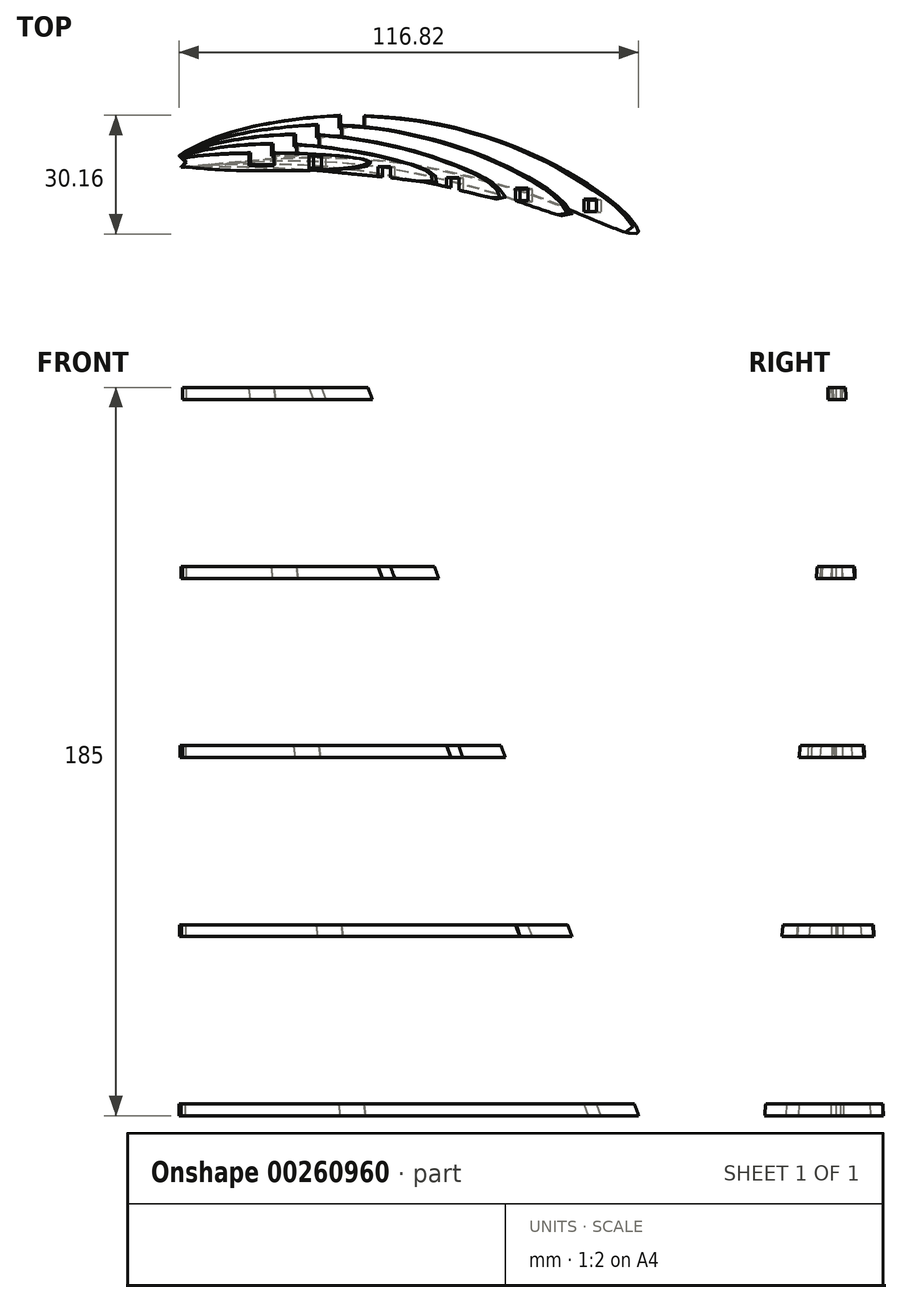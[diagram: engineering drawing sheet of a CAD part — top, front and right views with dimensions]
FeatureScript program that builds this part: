
annotation { "Feature Type Name" : "Feature", "Feature Type Description" : "" }
export const myFeature = defineFeature(function(context is Context, id is Id, definition is map)
    precondition{}
    {
        {
            var Q0;
            Q0=qCreatedBy(makeId("Top.planeOp"),FACE);
            var sketch = newSketch(context, id + "F0", { "sketchPlane" : qUnion([Q0])});
            skLineSegment(sketch, "E0", {"start": v(1.44, 1.44) * mm, "end": v(1.92, 1.72) * mm});
            skLineSegment(sketch, "E1", {"start": v(1.92, 1.72) * mm, "end": v(2.36, 1.99) * mm});
            skLineSegment(sketch, "E2", {"start": v(2.36, 1.99) * mm, "end": v(2.79, 2.25) * mm});
            skLineSegment(sketch, "E3", {"start": v(2.79, 2.25) * mm, "end": v(3.2, 2.5) * mm});
            skLineSegment(sketch, "E4", {"start": v(3.2, 2.5) * mm, "end": v(4, 2.98) * mm});
            skLineSegment(sketch, "E5", {"start": v(4, 2.98) * mm, "end": v(4.43, 3.23) * mm});
            skLineSegment(sketch, "E6", {"start": v(4.43, 3.23) * mm, "end": v(5.66, 3.88) * mm});
            skLineSegment(sketch, "E7", {"start": v(5.66, 3.88) * mm, "end": v(6.55, 4.3) * mm});
            skLineSegment(sketch, "E8", {"start": v(6.55, 4.3) * mm, "end": v(7.46, 4.72) * mm});
            skLineSegment(sketch, "E9", {"start": v(7.46, 4.72) * mm, "end": v(8.73, 5.26) * mm});
            skLineSegment(sketch, "E10", {"start": v(8.73, 5.26) * mm, "end": v(9.3, 5.5) * mm});
            skLineSegment(sketch, "E11", {"start": v(9.3, 5.5) * mm, "end": v(10.22, 5.87) * mm});
            skLineSegment(sketch, "E12", {"start": v(10.22, 5.87) * mm, "end": v(11.14, 6.22) * mm});
            skLineSegment(sketch, "E13", {"start": v(11.14, 6.22) * mm, "end": v(12.07, 6.56) * mm});
            skLineSegment(sketch, "E14", {"start": v(12.07, 6.56) * mm, "end": v(12.99, 6.88) * mm});
            skLineSegment(sketch, "E15", {"start": v(12.99, 6.88) * mm, "end": v(14.24, 7.3) * mm});
            skLineSegment(sketch, "E16", {"start": v(14.24, 7.3) * mm, "end": v(14.85, 7.5) * mm});
            skLineSegment(sketch, "E17", {"start": v(14.85, 7.5) * mm, "end": v(15.79, 7.78) * mm});
            skLineSegment(sketch, "E18", {"start": v(15.79, 7.78) * mm, "end": v(17.68, 8.31) * mm});
            skLineSegment(sketch, "E19", {"start": v(17.68, 8.31) * mm, "end": v(19.6, 8.8) * mm});
            skLineSegment(sketch, "E20", {"start": v(19.6, 8.8) * mm, "end": v(20.82, 9.1) * mm});
            skLineSegment(sketch, "E21", {"start": v(20.82, 9.1) * mm, "end": v(23.44, 9.66) * mm});
            skLineSegment(sketch, "E22", {"start": v(23.44, 9.66) * mm, "end": v(25.37, 10.04) * mm});
            skLineSegment(sketch, "E23", {"start": v(25.37, 10.04) * mm, "end": v(28.23, 10.53) * mm});
            skLineSegment(sketch, "E24", {"start": v(28.23, 10.53) * mm, "end": v(29.26, 10.68) * mm});
            skLineSegment(sketch, "E25", {"start": v(29.26, 10.68) * mm, "end": v(31.2, 10.95) * mm});
            skLineSegment(sketch, "E26", {"start": v(31.2, 10.95) * mm, "end": v(33.16, 11.18) * mm});
            skLineSegment(sketch, "E27", {"start": v(33.16, 11.18) * mm, "end": v(35.12, 11.38) * mm});
            skLineSegment(sketch, "E28", {"start": v(35.12, 11.38) * mm, "end": v(36.25, 11.48) * mm});
            skLineSegment(sketch, "E29", {"start": v(36.25, 11.48) * mm, "end": v(39.05, 11.7) * mm});
            skLineSegment(sketch, "E30", {"start": v(39.05, 11.7) * mm, "end": v(41.01, 11.83) * mm});
            skLineSegment(sketch, "E31", {"start": v(41.01, 11.83) * mm, "end": v(42.98, 11.92) * mm});
            skLineSegment(sketch, "E32", {"start": v(42.98, 11.92) * mm, "end": v(44.74, 11.96) * mm});
            skLineSegment(sketch, "E33", {"start": v(44.74, 11.96) * mm, "end": v(46.91, 11.97) * mm});
            skLineSegment(sketch, "E34", {"start": v(46.91, 11.97) * mm, "end": v(48.88, 11.94) * mm});
            skLineSegment(sketch, "E35", {"start": v(48.88, 11.94) * mm, "end": v(50.85, 11.87) * mm});
            skLineSegment(sketch, "E36", {"start": v(50.85, 11.87) * mm, "end": v(53.48, 11.72) * mm});
            skLineSegment(sketch, "E37", {"start": v(53.48, 11.72) * mm, "end": v(54.78, 11.63) * mm});
            skLineSegment(sketch, "E38", {"start": v(54.78, 11.63) * mm, "end": v(56.74, 11.45) * mm});
            skLineSegment(sketch, "E39", {"start": v(56.74, 11.45) * mm, "end": v(58.7, 11.24) * mm});
            skLineSegment(sketch, "E40", {"start": v(58.7, 11.24) * mm, "end": v(60.65, 11) * mm});
            skLineSegment(sketch, "E41", {"start": v(60.65, 11) * mm, "end": v(62.2, 10.77) * mm});
            skLineSegment(sketch, "E42", {"start": v(62.2, 10.77) * mm, "end": v(64.54, 10.39) * mm});
            skLineSegment(sketch, "E43", {"start": v(64.54, 10.39) * mm, "end": v(66.48, 10.03) * mm});
            skLineSegment(sketch, "E44", {"start": v(66.48, 10.03) * mm, "end": v(68.41, 9.64) * mm});
            skLineSegment(sketch, "E45", {"start": v(68.41, 9.64) * mm, "end": v(70.94, 9.1) * mm});
            skLineSegment(sketch, "E46", {"start": v(70.94, 9.1) * mm, "end": v(72.26, 8.78) * mm});
            skLineSegment(sketch, "E47", {"start": v(72.26, 8.78) * mm, "end": v(74.17, 8.31) * mm});
            skLineSegment(sketch, "E48", {"start": v(74.17, 8.31) * mm, "end": v(76.07, 7.8) * mm});
            skLineSegment(sketch, "E49", {"start": v(76.07, 7.8) * mm, "end": v(77.96, 7.27) * mm});
            skLineSegment(sketch, "E50", {"start": v(77.96, 7.27) * mm, "end": v(79.44, 6.82) * mm});
            skLineSegment(sketch, "E51", {"start": v(79.44, 6.82) * mm, "end": v(81.71, 6.07) * mm});
            skLineSegment(sketch, "E52", {"start": v(81.71, 6.07) * mm, "end": v(83.57, 5.42) * mm});
            skLineSegment(sketch, "E53", {"start": v(83.57, 5.42) * mm, "end": v(85.42, 4.73) * mm});
            skLineSegment(sketch, "E54", {"start": v(85.42, 4.73) * mm, "end": v(87.45, 3.95) * mm});
            skLineSegment(sketch, "E55", {"start": v(87.45, 3.95) * mm, "end": v(89.08, 3.3) * mm});
            skLineSegment(sketch, "E56", {"start": v(89.08, 3.3) * mm, "end": v(90.9, 2.53) * mm});
            skLineSegment(sketch, "E57", {"start": v(90.9, 2.53) * mm, "end": v(92.7, 1.74) * mm});
            skLineSegment(sketch, "E58", {"start": v(92.7, 1.74) * mm, "end": v(94.87, 0.72) * mm});
            skLineSegment(sketch, "E59", {"start": v(94.87, 0.72) * mm, "end": v(95.37, 0.47) * mm});
            skLineSegment(sketch, "E60", {"start": v(95.37, 0.47) * mm, "end": v(96.24, 0.02) * mm});
            skLineSegment(sketch, "E61", {"start": v(96.24, 0.02) * mm, "end": v(97.98, -0.9) * mm});
            skLineSegment(sketch, "E62", {"start": v(97.98, -0.9) * mm, "end": v(99.7, -1.86) * mm});
            skLineSegment(sketch, "E63", {"start": v(99.7, -1.86) * mm, "end": v(101.45, -2.87) * mm});
            skLineSegment(sketch, "E64", {"start": v(101.45, -2.87) * mm, "end": v(103.1, -3.86) * mm});
            skLineSegment(sketch, "E65", {"start": v(103.1, -3.86) * mm, "end": v(104.78, -4.9) * mm});
            skLineSegment(sketch, "E66", {"start": v(104.78, -4.9) * mm, "end": v(107.19, -6.46) * mm});
            skLineSegment(sketch, "E67", {"start": v(107.19, -6.46) * mm, "end": v(108.06, -7.05) * mm});
            skLineSegment(sketch, "E68", {"start": v(108.06, -7.05) * mm, "end": v(109.65, -8.19) * mm});
            skLineSegment(sketch, "E69", {"start": v(109.65, -8.19) * mm, "end": v(111.97, -9.93) * mm});
            skLineSegment(sketch, "E70", {"start": v(111.97, -9.93) * mm, "end": v(112.82, -10.59) * mm});
            skLineSegment(sketch, "E71", {"start": v(112.82, -10.59) * mm, "end": v(113.6, -11.22) * mm});
            skLineSegment(sketch, "E72", {"start": v(113.6, -11.22) * mm, "end": v(114.35, -11.87) * mm});
            skLineSegment(sketch, "E73", {"start": v(114.35, -11.87) * mm, "end": v(114.71, -12.2) * mm});
            skLineSegment(sketch, "E74", {"start": v(114.71, -12.2) * mm, "end": v(115.06, -12.53) * mm});
            skLineSegment(sketch, "E75", {"start": v(115.06, -12.53) * mm, "end": v(115.4, -12.86) * mm});
            skLineSegment(sketch, "E76", {"start": v(115.4, -12.86) * mm, "end": v(115.56, -13.04) * mm});
            skLineSegment(sketch, "E77", {"start": v(115.56, -13.04) * mm, "end": v(116.33, -13.9) * mm});
            skLineSegment(sketch, "E78", {"start": v(116.33, -13.9) * mm, "end": v(116.63, -14.27) * mm});
            skLineSegment(sketch, "E79", {"start": v(116.63, -14.27) * mm, "end": v(116.94, -14.64) * mm});
            skLineSegment(sketch, "E80", {"start": v(116.94, -14.64) * mm, "end": v(117.27, -15.03) * mm});
            skLineSegment(sketch, "E81", {"start": v(117.27, -15.03) * mm, "end": v(117.62, -15.43) * mm});
            skLineSegment(sketch, "E82", {"start": v(117.62, -15.43) * mm, "end": v(117.84, -15.67) * mm});
            skLineSegment(sketch, "E83", {"start": v(117.84, -15.67) * mm, "end": v(118.38, -16.28) * mm});
            skLineSegment(sketch, "E84", {"start": v(118.38, -16.28) * mm, "end": v(118.54, -16.5) * mm});
            skLineSegment(sketch, "E85", {"start": v(118.54, -16.5) * mm, "end": v(118.68, -16.72) * mm});
            skLineSegment(sketch, "E86", {"start": v(118.68, -16.72) * mm, "end": v(118.78, -16.94) * mm});
            skLineSegment(sketch, "E87", {"start": v(118.78, -16.94) * mm, "end": v(118.8, -17.05) * mm});
            skLineSegment(sketch, "E88", {"start": v(118.8, -17.05) * mm, "end": v(118.83, -17.16) * mm});
            skLineSegment(sketch, "E89", {"start": v(118.83, -17.16) * mm, "end": v(118.83, -17.27) * mm});
            skLineSegment(sketch, "E90", {"start": v(118.83, -17.27) * mm, "end": v(118.82, -17.37) * mm});
            skLineSegment(sketch, "E91", {"start": v(118.82, -17.37) * mm, "end": v(118.8, -17.47) * mm});
            skLineSegment(sketch, "E92", {"start": v(118.8, -17.47) * mm, "end": v(118.74, -17.59) * mm});
            skLineSegment(sketch, "E93", {"start": v(118.74, -17.59) * mm, "end": v(118.68, -17.7) * mm});
            skLineSegment(sketch, "E94", {"start": v(118.68, -17.7) * mm, "end": v(118.6, -17.8) * mm});
            skLineSegment(sketch, "E95", {"start": v(118.6, -17.8) * mm, "end": v(118.42, -17.97) * mm});
            skLineSegment(sketch, "E96", {"start": v(118.42, -17.97) * mm, "end": v(118.2, -18.12) * mm});
            skLineSegment(sketch, "E97", {"start": v(118.2, -18.12) * mm, "end": v(118.08, -18.18) * mm});
            skLineSegment(sketch, "E98", {"start": v(118.08, -18.18) * mm, "end": v(117.74, -18.28) * mm});
            skLineSegment(sketch, "E99", {"start": v(117.74, -18.28) * mm, "end": v(117.5, -18.3) * mm});
            skLineSegment(sketch, "E100", {"start": v(117.5, -18.3) * mm, "end": v(117.26, -18.27) * mm});
            skLineSegment(sketch, "E101", {"start": v(117.26, -18.27) * mm, "end": v(117.02, -18.22) * mm});
            skLineSegment(sketch, "E102", {"start": v(117.02, -18.22) * mm, "end": v(116.78, -18.14) * mm});
            skLineSegment(sketch, "E103", {"start": v(116.78, -18.14) * mm, "end": v(116.53, -18.04) * mm});
            skLineSegment(sketch, "E104", {"start": v(116.53, -18.04) * mm, "end": v(115.8, -17.7) * mm});
            skLineSegment(sketch, "E105", {"start": v(115.8, -17.7) * mm, "end": v(115.08, -17.39) * mm});
            skLineSegment(sketch, "E106", {"start": v(115.08, -17.39) * mm, "end": v(114.61, -17.2) * mm});
            skLineSegment(sketch, "E107", {"start": v(114.61, -17.2) * mm, "end": v(113.69, -16.86) * mm});
            skLineSegment(sketch, "E108", {"start": v(113.69, -16.86) * mm, "end": v(112.78, -16.55) * mm});
            skLineSegment(sketch, "E109", {"start": v(112.78, -16.55) * mm, "end": v(111.62, -16.15) * mm});
            skLineSegment(sketch, "E110", {"start": v(111.62, -16.15) * mm, "end": v(110.97, -15.92) * mm});
            skLineSegment(sketch, "E111", {"start": v(110.97, -15.92) * mm, "end": v(110.06, -15.57) * mm});
            skLineSegment(sketch, "E112", {"start": v(110.06, -15.57) * mm, "end": v(109.16, -15.2) * mm});
            skLineSegment(sketch, "E113", {"start": v(109.16, -15.2) * mm, "end": v(107.33, -14.42) * mm});
            skLineSegment(sketch, "E114", {"start": v(107.33, -14.42) * mm, "end": v(105.28, -13.52) * mm});
            skLineSegment(sketch, "E115", {"start": v(105.28, -13.52) * mm, "end": v(103.7, -12.84) * mm});
            skLineSegment(sketch, "E116", {"start": v(103.7, -12.84) * mm, "end": v(101.88, -12.07) * mm});
            skLineSegment(sketch, "E117", {"start": v(101.88, -12.07) * mm, "end": v(100.06, -11.33) * mm});
            skLineSegment(sketch, "E118", {"start": v(100.06, -11.33) * mm, "end": v(98.23, -10.6) * mm});
            skLineSegment(sketch, "E119", {"start": v(98.23, -10.6) * mm, "end": v(96.78, -10.05) * mm});
            skLineSegment(sketch, "E120", {"start": v(96.78, -10.05) * mm, "end": v(94.55, -9.23) * mm});
            skLineSegment(sketch, "E121", {"start": v(94.55, -9.23) * mm, "end": v(92.7, -8.57) * mm});
            skLineSegment(sketch, "E122", {"start": v(92.7, -8.57) * mm, "end": v(90.84, -7.93) * mm});
            skLineSegment(sketch, "E123", {"start": v(90.84, -7.93) * mm, "end": v(88.96, -7.31) * mm});
            skLineSegment(sketch, "E124", {"start": v(88.96, -7.31) * mm, "end": v(86.25, -6.46) * mm});
            skLineSegment(sketch, "E125", {"start": v(86.25, -6.46) * mm, "end": v(85.2, -6.14) * mm});
            skLineSegment(sketch, "E126", {"start": v(85.2, -6.14) * mm, "end": v(83.31, -5.58) * mm});
            skLineSegment(sketch, "E127", {"start": v(83.31, -5.58) * mm, "end": v(81.42, -5.04) * mm});
            skLineSegment(sketch, "E128", {"start": v(81.42, -5.04) * mm, "end": v(79.52, -4.52) * mm});
            skLineSegment(sketch, "E129", {"start": v(79.52, -4.52) * mm, "end": v(77.62, -4.02) * mm});
            skLineSegment(sketch, "E130", {"start": v(77.62, -4.02) * mm, "end": v(75.7, -3.54) * mm});
            skLineSegment(sketch, "E131", {"start": v(75.7, -3.54) * mm, "end": v(73.93, -3.11) * mm});
            skLineSegment(sketch, "E132", {"start": v(73.93, -3.11) * mm, "end": v(71.88, -2.64) * mm});
            skLineSegment(sketch, "E133", {"start": v(71.88, -2.64) * mm, "end": v(69.95, -2.21) * mm});
            skLineSegment(sketch, "E134", {"start": v(69.95, -2.21) * mm, "end": v(68.03, -1.81) * mm});
            skLineSegment(sketch, "E135", {"start": v(68.03, -1.81) * mm, "end": v(66.1, -1.43) * mm});
            skLineSegment(sketch, "E136", {"start": v(66.1, -1.43) * mm, "end": v(64.16, -1.08) * mm});
            skLineSegment(sketch, "E137", {"start": v(64.16, -1.08) * mm, "end": v(62.22, -0.75) * mm});
            skLineSegment(sketch, "E138", {"start": v(62.22, -0.75) * mm, "end": v(60.53, -0.48) * mm});
            skLineSegment(sketch, "E139", {"start": v(60.53, -0.48) * mm, "end": v(58.32, -0.16) * mm});
            skLineSegment(sketch, "E140", {"start": v(58.32, -0.16) * mm, "end": v(56.37, 0.1) * mm});
            skLineSegment(sketch, "E141", {"start": v(56.37, 0.1) * mm, "end": v(54.41, 0.33) * mm});
            skLineSegment(sketch, "E142", {"start": v(54.41, 0.33) * mm, "end": v(52.46, 0.54) * mm});
            skLineSegment(sketch, "E143", {"start": v(52.46, 0.54) * mm, "end": v(50.5, 0.72) * mm});
            skLineSegment(sketch, "E144", {"start": v(50.5, 0.72) * mm, "end": v(48.53, 0.87) * mm});
            skLineSegment(sketch, "E145", {"start": v(48.53, 0.87) * mm, "end": v(47.13, 0.96) * mm});
            skLineSegment(sketch, "E146", {"start": v(47.13, 0.96) * mm, "end": v(44.6, 1.09) * mm});
            skLineSegment(sketch, "E147", {"start": v(44.6, 1.09) * mm, "end": v(42.63, 1.15) * mm});
            skLineSegment(sketch, "E148", {"start": v(42.63, 1.15) * mm, "end": v(40.66, 1.2) * mm});
            skLineSegment(sketch, "E149", {"start": v(40.66, 1.2) * mm, "end": v(38.7, 1.22) * mm});
            skLineSegment(sketch, "E150", {"start": v(38.7, 1.22) * mm, "end": v(36.73, 1.22) * mm});
            skLineSegment(sketch, "E151", {"start": v(36.73, 1.22) * mm, "end": v(34.33, 1.2) * mm});
            skLineSegment(sketch, "E152", {"start": v(34.33, 1.2) * mm, "end": v(32.79, 1.17) * mm});
            skLineSegment(sketch, "E153", {"start": v(32.79, 1.17) * mm, "end": v(30.82, 1.11) * mm});
            skLineSegment(sketch, "E154", {"start": v(30.82, 1.11) * mm, "end": v(28.85, 1.04) * mm});
            skLineSegment(sketch, "E155", {"start": v(28.85, 1.04) * mm, "end": v(26.88, 0.94) * mm});
            skLineSegment(sketch, "E156", {"start": v(26.88, 0.94) * mm, "end": v(24.92, 0.83) * mm});
            skLineSegment(sketch, "E157", {"start": v(24.92, 0.83) * mm, "end": v(23.2, 0.72) * mm});
            skLineSegment(sketch, "E158", {"start": v(23.2, 0.72) * mm, "end": v(21, 0.55) * mm});
            skLineSegment(sketch, "E159", {"start": v(21, 0.55) * mm, "end": v(19.04, 0.38) * mm});
            skLineSegment(sketch, "E160", {"start": v(19.04, 0.38) * mm, "end": v(17.08, 0.2) * mm});
            skLineSegment(sketch, "E161", {"start": v(17.08, 0.2) * mm, "end": v(15.12, -0.01) * mm});
            skLineSegment(sketch, "E162", {"start": v(15.12, -0.01) * mm, "end": v(14.12, -0.12) * mm});
            skLineSegment(sketch, "E163", {"start": v(14.12, -0.12) * mm, "end": v(11.18, -0.45) * mm});
            skLineSegment(sketch, "E164", {"start": v(11.18, -0.45) * mm, "end": v(9.22, -0.66) * mm});
            skLineSegment(sketch, "E165", {"start": v(9.22, -0.66) * mm, "end": v(7.3, -0.84) * mm});
            skLineSegment(sketch, "E166", {"start": v(7.3, -0.84) * mm, "end": v(5.37, -0.99) * mm});
            skLineSegment(sketch, "E167", {"start": v(5.37, -0.99) * mm, "end": v(4.4, -1.06) * mm});
            skLineSegment(sketch, "E168", {"start": v(4.4, -1.06) * mm, "end": v(3.4, -1.14) * mm});
            skLineSegment(sketch, "E169", {"start": v(3.4, -1.14) * mm, "end": v(2.75, -1.2) * mm});
            skLineSegment(sketch, "E170", {"start": v(2.75, -1.2) * mm, "end": v(1.83, -1.25) * mm});
            skLineSegment(sketch, "E171", {"start": v(1.83, -1.25) * mm, "end": v(1.57, -1.25) * mm});
            skLineSegment(sketch, "E172", {"start": v(1.57, -1.25) * mm, "end": v(1.33, -1.22) * mm});
            skLineSegment(sketch, "E173", {"start": v(1.33, -1.22) * mm, "end": v(1.09, -1.16) * mm});
            skLineSegment(sketch, "E174", {"start": v(1.09, -1.16) * mm, "end": v(0.86, -1.08) * mm});
            skLineSegment(sketch, "E175", {"start": v(0.86, -1.08) * mm, "end": v(0.64, -0.96) * mm});
            skLineSegment(sketch, "E176", {"start": v(0.64, -0.96) * mm, "end": v(0.48, -0.84) * mm});
            skLineSegment(sketch, "E177", {"start": v(0.48, -0.84) * mm, "end": v(0.27, -0.62) * mm});
            skLineSegment(sketch, "E178", {"start": v(0.27, -0.62) * mm, "end": v(0.13, -0.4) * mm});
            skLineSegment(sketch, "E179", {"start": v(0.13, -0.4) * mm, "end": v(0.07, -0.28) * mm});
            skLineSegment(sketch, "E180", {"start": v(0.07, -0.28) * mm, "end": v(0.03, -0.17) * mm});
            skLineSegment(sketch, "E181", {"start": v(0.03, -0.17) * mm, "end": v(0, 0) * mm});
            skLineSegment(sketch, "E182", {"start": v(0, 0) * mm, "end": v(0, 0.05) * mm});
            skLineSegment(sketch, "E183", {"start": v(0, 0.05) * mm, "end": v(0, 0.16) * mm});
            skLineSegment(sketch, "E184", {"start": v(0, 0.16) * mm, "end": v(0.04, 0.26) * mm});
            skLineSegment(sketch, "E185", {"start": v(0.04, 0.26) * mm, "end": v(0.08, 0.36) * mm});
            skLineSegment(sketch, "E186", {"start": v(0.08, 0.36) * mm, "end": v(0.13, 0.46) * mm});
            skLineSegment(sketch, "E187", {"start": v(0.13, 0.46) * mm, "end": v(0.28, 0.65) * mm});
            skLineSegment(sketch, "E188", {"start": v(0.28, 0.65) * mm, "end": v(0.47, 0.82) * mm});
            skLineSegment(sketch, "E189", {"start": v(0.47, 0.82) * mm, "end": v(0.7, 0.98) * mm});
            skLineSegment(sketch, "E190", {"start": v(0.7, 0.98) * mm, "end": v(0.93, 1.14) * mm});
            skLineSegment(sketch, "E191", {"start": v(0.93, 1.14) * mm, "end": v(1.44, 1.44) * mm});
            skSolve(sketch);
        }
        {
            var Q0;
            Q0=qCreatedBy(makeId("Top.planeOp"),FACE);
            var sketch = newSketch(context, id + "F1", { "sketchPlane" : qUnion([Q0])});
            skPoint(sketch, "E192.0", {"position": v(0, 0) * mm});
            skPoint(sketch, "E192.1", {"position": v(0, 0.16) * mm});
            skPoint(sketch, "E192.2", {"position": v(0.13, 0.46) * mm});
            skPoint(sketch, "E192.3", {"position": v(1.44, 1.44) * mm});
            skPoint(sketch, "E192.4", {"position": v(10.22, 5.87) * mm});
            skPoint(sketch, "E192.5", {"position": v(23.44, 9.66) * mm});
            skPoint(sketch, "E192.6", {"position": v(36.25, 11.48) * mm});
            skPoint(sketch, "E192.7", {"position": v(46.91, 11.97) * mm});
            skPoint(sketch, "E192.8", {"position": v(64.54, 10.39) * mm});
            skPoint(sketch, "E192.9", {"position": v(79.44, 6.82) * mm});
            skPoint(sketch, "E192.10", {"position": v(101.45, -2.87) * mm});
            skPoint(sketch, "E192.11", {"position": v(108.06, -7.05) * mm});
            skPoint(sketch, "E192.12", {"position": v(118.8, -17.47) * mm});
            skPoint(sketch, "E192.13", {"position": v(118.6, -17.8) * mm});
            skPoint(sketch, "E192.14", {"position": v(118.08, -18.18) * mm});
            skPoint(sketch, "E192.15", {"position": v(96.78, -10.05) * mm});
            skPoint(sketch, "E192.16", {"position": v(83.31, -5.58) * mm});
            skPoint(sketch, "E192.17", {"position": v(66.1, -1.43) * mm});
            skPoint(sketch, "E192.18", {"position": v(52.46, 0.54) * mm});
            skPoint(sketch, "E192.19", {"position": v(36.73, 1.22) * mm});
            skPoint(sketch, "E192.20", {"position": v(24.92, 0.83) * mm});
            skPoint(sketch, "E192.21", {"position": v(11.18, -0.45) * mm});
            skPoint(sketch, "E192.22", {"position": v(0.64, -0.96) * mm});
            skPoint(sketch, "E192.23", {"position": v(0.13, -0.4) * mm});
            skPoint(sketch, "E192.24", {"position": v(0.03, -0.17) * mm});
            skPoint(sketch, "E192.25", {"position": v(91.8, 2.14) * mm});
            skPoint(sketch, "E192.26", {"position": v(115.48, -12.95) * mm});
            skPoint(sketch, "E192.27", {"position": v(110.52, -15.74) * mm});
            skPoint(sketch, "E192.28", {"position": v(1.7, -1.25) * mm});
            skFitSpline(sketch, "E193", {"points": [v(0, 0) * mm, v(0, 0.16) * mm, v(0.13, 0.46) * mm, v(1.44, 1.44) * mm, v(10.22, 5.87) * mm, v(23.44, 9.66) * mm, v(36.25, 11.48) * mm, v(46.91, 11.97) * mm, v(64.54, 10.39) * mm, v(79.44, 6.82) * mm, v(91.8, 2.14) * mm, v(101.45, -2.87) * mm, v(108.06, -7.05) * mm, v(115.48, -12.95) * mm, v(118.8, -17.47) * mm, v(118.6, -17.8) * mm, v(118.08, -18.18) * mm, v(110.52, -15.74) * mm, v(96.78, -10.05) * mm, v(83.31, -5.58) * mm, v(66.1, -1.43) * mm, v(52.46, 0.54) * mm, v(36.73, 1.22) * mm, v(24.92, 0.83) * mm, v(11.18, -0.45) * mm, v(1.7, -1.25) * mm, v(0.64, -1.04) * mm, v(0.13, -0.4) * mm, v(0.03, -0.17) * mm, v(0, 0) * mm]});
            skSolve(sketch);
        }
        {
            var Q0;
            Q0=qCreatedBy(makeId("Top.planeOp"),FACE);
            cPlane(context, id + "F2", {"entities" : qUnion([Q0]), "cplaneType" : CPlaneType.OFFSET, "offset" : 185 * mm, "width" : 150 * mm, "height" : 150 * mm});
        }
        {
            var Q0;
            Q0=qCreatedBy(id+"F2.planeOp",FACE);
            var sketch = newSketch(context, id + "F3", { "sketchPlane" : qUnion([Q0])});
            skLineSegment(sketch, "E194", {"start": v(0, 0) * mm, "end": v(0.13, 0.15) * mm});
            skLineSegment(sketch, "E195", {"start": v(0.13, 0.15) * mm, "end": v(0.27, 0.3) * mm});
            skLineSegment(sketch, "E196", {"start": v(0.27, 0.3) * mm, "end": v(0.34, 0.36) * mm});
            skLineSegment(sketch, "E197", {"start": v(0.34, 0.36) * mm, "end": v(0.4, 0.4) * mm});
            skLineSegment(sketch, "E198", {"start": v(0.4, 0.4) * mm, "end": v(0.5, 0.47) * mm});
            skLineSegment(sketch, "E199", {"start": v(0.5, 0.47) * mm, "end": v(0.59, 0.52) * mm});
            skLineSegment(sketch, "E200", {"start": v(0.59, 0.52) * mm, "end": v(0.67, 0.56) * mm});
            skLineSegment(sketch, "E201", {"start": v(0.67, 0.56) * mm, "end": v(0.76, 0.6) * mm});
            skLineSegment(sketch, "E202", {"start": v(0.76, 0.6) * mm, "end": v(0.95, 0.66) * mm});
            skLineSegment(sketch, "E203", {"start": v(0.95, 0.66) * mm, "end": v(1.15, 0.71) * mm});
            skLineSegment(sketch, "E204", {"start": v(1.15, 0.71) * mm, "end": v(1.54, 0.8) * mm});
            skLineSegment(sketch, "E205", {"start": v(1.54, 0.8) * mm, "end": v(1.74, 0.84) * mm});
            skLineSegment(sketch, "E206", {"start": v(1.74, 0.84) * mm, "end": v(2.14, 0.91) * mm});
            skLineSegment(sketch, "E207", {"start": v(2.14, 0.91) * mm, "end": v(2.9, 1.06) * mm});
            skLineSegment(sketch, "E208", {"start": v(2.9, 1.06) * mm, "end": v(3.39, 1.15) * mm});
            skLineSegment(sketch, "E209", {"start": v(3.39, 1.15) * mm, "end": v(4.46, 1.31) * mm});
            skLineSegment(sketch, "E210", {"start": v(4.46, 1.31) * mm, "end": v(5.25, 1.41) * mm});
            skLineSegment(sketch, "E211", {"start": v(5.25, 1.41) * mm, "end": v(5.93, 1.5) * mm});
            skLineSegment(sketch, "E212", {"start": v(5.93, 1.5) * mm, "end": v(6.82, 1.6) * mm});
            skLineSegment(sketch, "E213", {"start": v(6.82, 1.6) * mm, "end": v(7.6, 1.67) * mm});
            skLineSegment(sketch, "E214", {"start": v(7.6, 1.67) * mm, "end": v(9.01, 1.8) * mm});
            skLineSegment(sketch, "E215", {"start": v(9.01, 1.8) * mm, "end": v(10.76, 1.93) * mm});
            skLineSegment(sketch, "E216", {"start": v(10.76, 1.93) * mm, "end": v(11.55, 1.98) * mm});
            skLineSegment(sketch, "E217", {"start": v(11.55, 1.98) * mm, "end": v(12.55, 2.04) * mm});
            skLineSegment(sketch, "E218", {"start": v(12.55, 2.04) * mm, "end": v(13.13, 2.07) * mm});
            skLineSegment(sketch, "E219", {"start": v(13.13, 2.07) * mm, "end": v(13.92, 2.1) * mm});
            skLineSegment(sketch, "E220", {"start": v(13.92, 2.1) * mm, "end": v(15.5, 2.16) * mm});
            skLineSegment(sketch, "E221", {"start": v(15.5, 2.16) * mm, "end": v(16.48, 2.2) * mm});
            skLineSegment(sketch, "E222", {"start": v(16.48, 2.2) * mm, "end": v(18.66, 2.25) * mm});
            skLineSegment(sketch, "E223", {"start": v(18.66, 2.25) * mm, "end": v(20.72, 2.3) * mm});
            skLineSegment(sketch, "E224", {"start": v(20.72, 2.3) * mm, "end": v(23.4, 2.33) * mm});
            skLineSegment(sketch, "E225", {"start": v(23.4, 2.33) * mm, "end": v(25, 2.34) * mm});
            skLineSegment(sketch, "E226", {"start": v(25, 2.34) * mm, "end": v(26.56, 2.33) * mm});
            skLineSegment(sketch, "E227", {"start": v(26.56, 2.33) * mm, "end": v(29.28, 2.3) * mm});
            skLineSegment(sketch, "E228", {"start": v(29.28, 2.3) * mm, "end": v(31.3, 2.25) * mm});
            skLineSegment(sketch, "E229", {"start": v(31.3, 2.25) * mm, "end": v(33.52, 2.2) * mm});
            skLineSegment(sketch, "E230", {"start": v(33.52, 2.2) * mm, "end": v(34.46, 2.16) * mm});
            skLineSegment(sketch, "E231", {"start": v(34.46, 2.16) * mm, "end": v(36.04, 2.1) * mm});
            skLineSegment(sketch, "E232", {"start": v(36.04, 2.1) * mm, "end": v(36.83, 2.07) * mm});
            skLineSegment(sketch, "E233", {"start": v(36.83, 2.07) * mm, "end": v(37.45, 2.04) * mm});
            skLineSegment(sketch, "E234", {"start": v(37.45, 2.04) * mm, "end": v(38.41, 1.99) * mm});
            skLineSegment(sketch, "E235", {"start": v(38.41, 1.99) * mm, "end": v(39.2, 1.93) * mm});
            skLineSegment(sketch, "E236", {"start": v(39.2, 1.93) * mm, "end": v(40.99, 1.8) * mm});
            skLineSegment(sketch, "E237", {"start": v(40.99, 1.8) * mm, "end": v(42.35, 1.67) * mm});
            skLineSegment(sketch, "E238", {"start": v(42.35, 1.67) * mm, "end": v(43.14, 1.6) * mm});
            skLineSegment(sketch, "E239", {"start": v(43.14, 1.6) * mm, "end": v(44.08, 1.5) * mm});
            skLineSegment(sketch, "E240", {"start": v(44.08, 1.5) * mm, "end": v(44.7, 1.42) * mm});
            skLineSegment(sketch, "E241", {"start": v(44.7, 1.42) * mm, "end": v(45.49, 1.32) * mm});
            skLineSegment(sketch, "E242", {"start": v(45.49, 1.32) * mm, "end": v(46.61, 1.15) * mm});
            skLineSegment(sketch, "E243", {"start": v(46.61, 1.15) * mm, "end": v(47.06, 1.07) * mm});
            skLineSegment(sketch, "E244", {"start": v(47.06, 1.07) * mm, "end": v(47.46, 1) * mm});
            skLineSegment(sketch, "E245", {"start": v(47.46, 1) * mm, "end": v(47.85, 0.92) * mm});
            skLineSegment(sketch, "E246", {"start": v(47.85, 0.92) * mm, "end": v(48.23, 0.84) * mm});
            skLineSegment(sketch, "E247", {"start": v(48.23, 0.84) * mm, "end": v(48.46, 0.8) * mm});
            skLineSegment(sketch, "E248", {"start": v(48.46, 0.8) * mm, "end": v(48.78, 0.72) * mm});
            skLineSegment(sketch, "E249", {"start": v(48.78, 0.72) * mm, "end": v(48.96, 0.68) * mm});
            skLineSegment(sketch, "E250", {"start": v(48.96, 0.68) * mm, "end": v(49.14, 0.61) * mm});
            skLineSegment(sketch, "E251", {"start": v(49.14, 0.61) * mm, "end": v(49.33, 0.54) * mm});
            skLineSegment(sketch, "E252", {"start": v(49.33, 0.54) * mm, "end": v(49.43, 0.5) * mm});
            skLineSegment(sketch, "E253", {"start": v(49.43, 0.5) * mm, "end": v(49.53, 0.44) * mm});
            skLineSegment(sketch, "E254", {"start": v(49.53, 0.44) * mm, "end": v(49.6, 0.4) * mm});
            skLineSegment(sketch, "E255", {"start": v(49.6, 0.4) * mm, "end": v(49.73, 0.32) * mm});
            skLineSegment(sketch, "E256", {"start": v(49.73, 0.32) * mm, "end": v(49.83, 0.25) * mm});
            skLineSegment(sketch, "E257", {"start": v(49.83, 0.25) * mm, "end": v(49.91, 0.18) * mm});
            skLineSegment(sketch, "E258", {"start": v(49.91, 0.18) * mm, "end": v(49.94, 0.14) * mm});
            skLineSegment(sketch, "E259", {"start": v(49.94, 0.14) * mm, "end": v(49.97, 0.1) * mm});
            skLineSegment(sketch, "E260", {"start": v(49.97, 0.1) * mm, "end": v(49.99, 0.07) * mm});
            skLineSegment(sketch, "E261", {"start": v(49.99, 0.07) * mm, "end": v(50, 0.03) * mm});
            skLineSegment(sketch, "E262", {"start": v(50, 0.03) * mm, "end": v(50, 0) * mm});
            skLineSegment(sketch, "E263", {"start": v(50, 0) * mm, "end": v(50, -0.04) * mm});
            skLineSegment(sketch, "E264", {"start": v(50, -0.04) * mm, "end": v(49.97, -0.08) * mm});
            skLineSegment(sketch, "E265", {"start": v(49.97, -0.08) * mm, "end": v(49.95, -0.11) * mm});
            skLineSegment(sketch, "E266", {"start": v(49.95, -0.11) * mm, "end": v(49.92, -0.15) * mm});
            skLineSegment(sketch, "E267", {"start": v(49.92, -0.15) * mm, "end": v(49.88, -0.18) * mm});
            skLineSegment(sketch, "E268", {"start": v(49.88, -0.18) * mm, "end": v(49.79, -0.24) * mm});
            skLineSegment(sketch, "E269", {"start": v(49.79, -0.24) * mm, "end": v(49.69, -0.3) * mm});
            skLineSegment(sketch, "E270", {"start": v(49.69, -0.3) * mm, "end": v(49.6, -0.35) * mm});
            skLineSegment(sketch, "E271", {"start": v(49.6, -0.35) * mm, "end": v(49.48, -0.41) * mm});
            skLineSegment(sketch, "E272", {"start": v(49.48, -0.41) * mm, "end": v(49.38, -0.46) * mm});
            skLineSegment(sketch, "E273", {"start": v(49.38, -0.46) * mm, "end": v(49.19, -0.54) * mm});
            skLineSegment(sketch, "E274", {"start": v(49.19, -0.54) * mm, "end": v(49, -0.6) * mm});
            skLineSegment(sketch, "E275", {"start": v(49, -0.6) * mm, "end": v(48.83, -0.66) * mm});
            skLineSegment(sketch, "E276", {"start": v(48.83, -0.66) * mm, "end": v(48.5, -0.75) * mm});
            skLineSegment(sketch, "E277", {"start": v(48.5, -0.75) * mm, "end": v(48.29, -0.8) * mm});
            skLineSegment(sketch, "E278", {"start": v(48.29, -0.8) * mm, "end": v(47.9, -0.88) * mm});
            skLineSegment(sketch, "E279", {"start": v(47.9, -0.88) * mm, "end": v(47.52, -0.96) * mm});
            skLineSegment(sketch, "E280", {"start": v(47.52, -0.96) * mm, "end": v(47.12, -1.02) * mm});
            skLineSegment(sketch, "E281", {"start": v(47.12, -1.02) * mm, "end": v(46.66, -1.1) * mm});
            skLineSegment(sketch, "E282", {"start": v(46.66, -1.1) * mm, "end": v(46.32, -1.15) * mm});
            skLineSegment(sketch, "E283", {"start": v(46.32, -1.15) * mm, "end": v(45.54, -1.25) * mm});
            skLineSegment(sketch, "E284", {"start": v(45.54, -1.25) * mm, "end": v(44.76, -1.34) * mm});
            skLineSegment(sketch, "E285", {"start": v(44.76, -1.34) * mm, "end": v(44.17, -1.4) * mm});
            skLineSegment(sketch, "E286", {"start": v(44.17, -1.4) * mm, "end": v(43.19, -1.48) * mm});
            skLineSegment(sketch, "E287", {"start": v(43.19, -1.48) * mm, "end": v(42.4, -1.54) * mm});
            skLineSegment(sketch, "E288", {"start": v(42.4, -1.54) * mm, "end": v(41.09, -1.64) * mm});
            skLineSegment(sketch, "E289", {"start": v(41.09, -1.64) * mm, "end": v(39.24, -1.78) * mm});
            skLineSegment(sketch, "E290", {"start": v(39.24, -1.78) * mm, "end": v(38.45, -1.83) * mm});
            skLineSegment(sketch, "E291", {"start": v(38.45, -1.83) * mm, "end": v(37.5, -1.9) * mm});
            skLineSegment(sketch, "E292", {"start": v(37.5, -1.9) * mm, "end": v(36.88, -1.92) * mm});
            skLineSegment(sketch, "E293", {"start": v(36.88, -1.92) * mm, "end": v(36.09, -1.96) * mm});
            skLineSegment(sketch, "E294", {"start": v(36.09, -1.96) * mm, "end": v(33.57, -2.04) * mm});
            skLineSegment(sketch, "E295", {"start": v(33.57, -2.04) * mm, "end": v(31.35, -2.1) * mm});
            skLineSegment(sketch, "E296", {"start": v(31.35, -2.1) * mm, "end": v(29.76, -2.14) * mm});
            skLineSegment(sketch, "E297", {"start": v(29.76, -2.14) * mm, "end": v(29.33, -2.14) * mm});
            skLineSegment(sketch, "E298", {"start": v(29.33, -2.14) * mm, "end": v(28.18, -2.15) * mm});
            skLineSegment(sketch, "E299", {"start": v(28.18, -2.15) * mm, "end": v(25, -2.14) * mm});
            skLineSegment(sketch, "E300", {"start": v(25, -2.14) * mm, "end": v(21.86, -2.15) * mm});
            skLineSegment(sketch, "E301", {"start": v(21.86, -2.15) * mm, "end": v(20.67, -2.14) * mm});
            skLineSegment(sketch, "E302", {"start": v(20.67, -2.14) * mm, "end": v(18.7, -2.1) * mm});
            skLineSegment(sketch, "E303", {"start": v(18.7, -2.1) * mm, "end": v(16.43, -2.04) * mm});
            skLineSegment(sketch, "E304", {"start": v(16.43, -2.04) * mm, "end": v(13.96, -1.96) * mm});
            skLineSegment(sketch, "E305", {"start": v(13.96, -1.96) * mm, "end": v(13.17, -1.93) * mm});
            skLineSegment(sketch, "E306", {"start": v(13.17, -1.93) * mm, "end": v(12.5, -1.9) * mm});
            skLineSegment(sketch, "E307", {"start": v(12.5, -1.9) * mm, "end": v(11.59, -1.84) * mm});
            skLineSegment(sketch, "E308", {"start": v(11.59, -1.84) * mm, "end": v(10.8, -1.78) * mm});
            skLineSegment(sketch, "E309", {"start": v(10.8, -1.78) * mm, "end": v(8.91, -1.64) * mm});
            skLineSegment(sketch, "E310", {"start": v(8.91, -1.64) * mm, "end": v(7.65, -1.55) * mm});
            skLineSegment(sketch, "E311", {"start": v(7.65, -1.55) * mm, "end": v(6.86, -1.49) * mm});
            skLineSegment(sketch, "E312", {"start": v(6.86, -1.49) * mm, "end": v(5.83, -1.4) * mm});
            skLineSegment(sketch, "E313", {"start": v(5.83, -1.4) * mm, "end": v(5.28, -1.34) * mm});
            skLineSegment(sketch, "E314", {"start": v(5.28, -1.34) * mm, "end": v(4.5, -1.25) * mm});
            skLineSegment(sketch, "E315", {"start": v(4.5, -1.25) * mm, "end": v(3.71, -1.15) * mm});
            skLineSegment(sketch, "E316", {"start": v(3.71, -1.15) * mm, "end": v(3.34, -1.1) * mm});
            skLineSegment(sketch, "E317", {"start": v(3.34, -1.1) * mm, "end": v(2.94, -1.03) * mm});
            skLineSegment(sketch, "E318", {"start": v(2.94, -1.03) * mm, "end": v(2.55, -0.96) * mm});
            skLineSegment(sketch, "E319", {"start": v(2.55, -0.96) * mm, "end": v(2.16, -0.89) * mm});
            skLineSegment(sketch, "E320", {"start": v(2.16, -0.89) * mm, "end": v(1.77, -0.8) * mm});
            skLineSegment(sketch, "E321", {"start": v(1.77, -0.8) * mm, "end": v(1.5, -0.75) * mm});
            skLineSegment(sketch, "E322", {"start": v(1.5, -0.75) * mm, "end": v(1.18, -0.67) * mm});
            skLineSegment(sketch, "E323", {"start": v(1.18, -0.67) * mm, "end": v(1, -0.62) * mm});
            skLineSegment(sketch, "E324", {"start": v(1, -0.62) * mm, "end": v(0.8, -0.56) * mm});
            skLineSegment(sketch, "E325", {"start": v(0.8, -0.56) * mm, "end": v(0.62, -0.48) * mm});
            skLineSegment(sketch, "E326", {"start": v(0.62, -0.48) * mm, "end": v(0.53, -0.43) * mm});
            skLineSegment(sketch, "E327", {"start": v(0.53, -0.43) * mm, "end": v(0.45, -0.38) * mm});
            skLineSegment(sketch, "E328", {"start": v(0.45, -0.38) * mm, "end": v(0.4, -0.35) * mm});
            skLineSegment(sketch, "E329", {"start": v(0.4, -0.35) * mm, "end": v(0.3, -0.27) * mm});
            skLineSegment(sketch, "E330", {"start": v(0.3, -0.27) * mm, "end": v(0.14, -0.14) * mm});
            skLineSegment(sketch, "E331", {"start": v(0.14, -0.14) * mm, "end": v(0, 0) * mm});
            skSolve(sketch);
        }
        {
            var Q0;
            Q0=qCreatedBy(id+"F2.planeOp",FACE);
            var sketch = newSketch(context, id + "F4", { "sketchPlane" : qUnion([Q0])});
            skPoint(sketch, "E332.0", {"position": v(0, 0) * mm});
            skPoint(sketch, "E332.1", {"position": v(0.34, 0.36) * mm});
            skPoint(sketch, "E332.2", {"position": v(0.76, 0.6) * mm});
            skPoint(sketch, "E332.3", {"position": v(2.9, 1.06) * mm});
            skPoint(sketch, "E332.4", {"position": v(5.25, 1.41) * mm});
            skPoint(sketch, "E332.5", {"position": v(9.01, 1.8) * mm});
            skPoint(sketch, "E332.6", {"position": v(15.5, 2.16) * mm});
            skPoint(sketch, "E332.7", {"position": v(12.55, 2.04) * mm});
            skPoint(sketch, "E332.8", {"position": v(20.72, 2.3) * mm});
            skPoint(sketch, "E332.9", {"position": v(23.4, 2.33) * mm});
            skPoint(sketch, "E332.10", {"position": v(26.56, 2.33) * mm});
            skPoint(sketch, "E332.11", {"position": v(34.46, 2.16) * mm});
            skPoint(sketch, "E332.12", {"position": v(40.99, 1.8) * mm});
            skPoint(sketch, "E332.13", {"position": v(46.61, 1.15) * mm});
            skPoint(sketch, "E332.14", {"position": v(49.14, 0.61) * mm});
            skPoint(sketch, "E332.15", {"position": v(49.91, 0.18) * mm});
            skPoint(sketch, "E332.16", {"position": v(50, 0) * mm});
            skPoint(sketch, "E332.17", {"position": v(49.95, -0.11) * mm});
            skPoint(sketch, "E332.18", {"position": v(49.38, -0.46) * mm});
            skPoint(sketch, "E332.19", {"position": v(46.66, -1.1) * mm});
            skPoint(sketch, "E332.20", {"position": v(41.09, -1.64) * mm});
            skPoint(sketch, "E332.21", {"position": v(33.57, -2.04) * mm});
            skPoint(sketch, "E332.22", {"position": v(28.18, -2.15) * mm});
            skPoint(sketch, "E332.23", {"position": v(20.67, -2.14) * mm});
            skPoint(sketch, "E332.24", {"position": v(21.86, -2.15) * mm});
            skPoint(sketch, "E332.25", {"position": v(13.17, -1.93) * mm});
            skPoint(sketch, "E332.26", {"position": v(8.91, -1.64) * mm});
            skPoint(sketch, "E332.27", {"position": v(5.28, -1.34) * mm});
            skPoint(sketch, "E332.28", {"position": v(2.55, -0.96) * mm});
            skPoint(sketch, "E332.29", {"position": v(0.8, -0.56) * mm});
            skPoint(sketch, "E332.30", {"position": v(0.45, -0.38) * mm});
            skPoint(sketch, "E332.31", {"position": v(0.3, -0.27) * mm});
            skPoint(sketch, "E332.32", {"position": v(49.67, 0.36) * mm});
            skPoint(sketch, "E333.0", {"position": v(49.69, -0.3) * mm});
            skPoint(sketch, "E334.0", {"position": v(49.88, -0.18) * mm});
            skFitSpline(sketch, "E335", {"points": [v(0, 0) * mm, v(0.34, 0.36) * mm, v(0.76, 0.6) * mm, v(2.9, 1.06) * mm, v(5.25, 1.41) * mm, v(9.01, 1.8) * mm, v(12.55, 2.04) * mm, v(15.5, 2.16) * mm, v(20.72, 2.3) * mm, v(23.4, 2.33) * mm, v(26.56, 2.33) * mm, v(34.46, 2.16) * mm, v(40.99, 1.8) * mm, v(46.61, 1.15) * mm, v(49.14, 0.61) * mm, v(49.67, 0.36) * mm, v(49.91, 0.18) * mm, v(50, 0) * mm, v(49.95, -0.11) * mm, v(49.88, -0.18) * mm, v(49.69, -0.3) * mm, v(49.38, -0.46) * mm, v(46.66, -1.1) * mm, v(41.09, -1.64) * mm, v(33.57, -2.04) * mm, v(28.18, -2.15) * mm, v(21.86, -2.15) * mm, v(20.67, -2.14) * mm, v(13.17, -1.93) * mm, v(8.91, -1.64) * mm, v(5.28, -1.34) * mm, v(2.55, -0.96) * mm, v(0.8, -0.56) * mm, v(0.45, -0.38) * mm, v(0.3, -0.27) * mm, v(0, 0) * mm]});
            skSolve(sketch);
        }
        {
            var Q0;
            Q0=makeQuery(id+"F4.imprint","IMPRINT",FACE,{"disambiguationData":[TD([[makeQuery(id+"F4.imprint","IMPRINT",EDGE,{"derivedFrom":sQuery(id+"F4.wireOp",EDGE,"E335")}),-1.0]])]});
            var Q1;
            Q1=makeQuery(id+"F1.imprint","IMPRINT",FACE,{"disambiguationData":[TD([[makeQuery(id+"F1.imprint","IMPRINT",EDGE,{"derivedFrom":sQuery(id+"F1.wireOp",EDGE,"E193")}),-1.0]])]});
            loft(context, id + "F5", {"sheetProfilesArray" : [{ "sheetProfileEntities" : qUnion([Q0]) }, { "sheetProfileEntities" : qUnion([Q1]) }]});
        }
        {
            var Q0;
            Q0=qCreatedBy(makeId("Front.planeOp"),FACE);
            var sketch = newSketch(context, id + "F6", { "sketchPlane" : qUnion([Q0])});
            skLineSegment(sketch, "E336", {"start": v(-23, 0) * mm, "end": v(-23, 3) * mm, "construction": true});
            skLineSegment(sketch, "E337.bottom", {"start": v(-23, 3) * mm, "end": v(143.31, 3) * mm});
            skLineSegment(sketch, "E337.top", {"start": v(-23, 45.5) * mm, "end": v(143.31, 45.5) * mm});
            skLineSegment(sketch, "E337.left", {"start": v(-23, 3) * mm, "end": v(-23, 45.5) * mm});
            skLineSegment(sketch, "E337.right", {"start": v(143.31, 3) * mm, "end": v(143.31, 45.5) * mm});
            skLineSegment(sketch, "E338.0.1.0", {"start": v(-23, 48.5) * mm, "end": v(143.31, 48.5) * mm});
            skLineSegment(sketch, "E338.0.1.1", {"start": v(-23, 91) * mm, "end": v(143.31, 91) * mm});
            skLineSegment(sketch, "E338.0.1.2", {"start": v(-23, 48.5) * mm, "end": v(-23, 91) * mm});
            skLineSegment(sketch, "E338.0.1.3", {"start": v(143.31, 48.5) * mm, "end": v(143.31, 91) * mm});
            skLineSegment(sketch, "E338.0.1.4", {"start": v(-23, 45.5) * mm, "end": v(-23, 48.5) * mm, "construction": true});
            skLineSegment(sketch, "E338.0.2.0", {"start": v(-23, 94) * mm, "end": v(143.31, 94) * mm});
            skLineSegment(sketch, "E338.0.2.1", {"start": v(-23, 136.5) * mm, "end": v(143.31, 136.5) * mm});
            skLineSegment(sketch, "E338.0.2.2", {"start": v(-23, 94) * mm, "end": v(-23, 136.5) * mm});
            skLineSegment(sketch, "E338.0.2.3", {"start": v(143.31, 94) * mm, "end": v(143.31, 136.5) * mm});
            skLineSegment(sketch, "E338.0.2.4", {"start": v(-23, 91) * mm, "end": v(-23, 94) * mm, "construction": true});
            skLineSegment(sketch, "E338.0.3.0", {"start": v(-23, 139.5) * mm, "end": v(143.31, 139.5) * mm});
            skLineSegment(sketch, "E338.0.3.1", {"start": v(-23, 182) * mm, "end": v(143.31, 182) * mm});
            skLineSegment(sketch, "E338.0.3.2", {"start": v(-23, 139.5) * mm, "end": v(-23, 182) * mm});
            skLineSegment(sketch, "E338.0.3.3", {"start": v(143.31, 139.5) * mm, "end": v(143.31, 182) * mm});
            skLineSegment(sketch, "E338.0.3.4", {"start": v(-23, 136.5) * mm, "end": v(-23, 139.5) * mm, "construction": true});
            skLineSegment(sketch, "E338.direction1", {"start": v(-23, 0) * mm, "end": v(2.9, 0.6) * mm, "construction": true});
            skLineSegment(sketch, "E338.direction2", {"start": v(-23, 0) * mm, "end": v(-23, 45.5) * mm, "construction": true});
            skSolve(sketch);
        }
        {
            var Q0;
            Q0=qCreatedBy(makeId("Top.planeOp"),FACE);
            var sketch = newSketch(context, id + "F7", { "sketchPlane" : qUnion([Q0])});
            skLineSegment(sketch, "E339", {"start": v(43.02, 12) * mm, "end": v(49.37, 12) * mm});
            skLineSegment(sketch, "E340", {"start": v(49.37, 12) * mm, "end": v(49.37, 8.83) * mm});
            skLineSegment(sketch, "E341", {"start": v(49.37, 8.83) * mm, "end": v(43.02, 8.83) * mm});
            skLineSegment(sketch, "E342", {"start": v(43.02, 8.83) * mm, "end": v(43.02, 12) * mm});
            skSolve(sketch);
        }
        {
            var Q0;
            Q0=qCreatedBy(id+"F2.planeOp",FACE);
            var sketch = newSketch(context, id + "F8", { "sketchPlane" : qUnion([Q0])});
            skLineSegment(sketch, "E343.bottom", {"start": v(19.79, 2.38) * mm, "end": v(26.14, 2.38) * mm});
            skLineSegment(sketch, "E343.top", {"start": v(19.79, -0.8) * mm, "end": v(26.14, -0.8) * mm});
            skLineSegment(sketch, "E343.left", {"start": v(19.79, 2.38) * mm, "end": v(19.79, -0.8) * mm});
            skLineSegment(sketch, "E343.right", {"start": v(26.14, 2.38) * mm, "end": v(26.14, -0.8) * mm});
            skLineSegment(sketch, "E344.bottom", {"start": v(0, 1.59) * mm, "end": v(3.18, 1.59) * mm});
            skLineSegment(sketch, "E344.top", {"start": v(0, -1.59) * mm, "end": v(3.18, -1.59) * mm});
            skLineSegment(sketch, "E344.left", {"start": v(0, 1.59) * mm, "end": v(0, -1.59) * mm});
            skLineSegment(sketch, "E344.right", {"start": v(3.18, 1.59) * mm, "end": v(3.18, -1.59) * mm});
            skSolve(sketch);
        }
        {
            var Q1;
            Q1=makeQuery(id+"F7.imprint","IMPRINT",FACE,{"disambiguationData":[TD([[makeQuery(id+"F7.imprint","IMPRINT",EDGE,{"derivedFrom":sQuery(id+"F7.wireOp",EDGE,"E339")}),-1.0]])]});
            var Q2;
            Q2=makeQuery(id+"F8.imprint","IMPRINT",FACE,{"disambiguationData":[TD([[makeQuery(id+"F8.imprint","IMPRINT",EDGE,{"derivedFrom":sQuery(id+"F8.wireOp",EDGE,"E343.bottom")}),-1.0]])]});
            loft(context, id + "F9", {"operationType" : NewBodyOperationType.REMOVE, "sheetProfilesArray" : [{ "sheetProfileEntities" : qUnion([Q1]) }, { "sheetProfileEntities" : qUnion([Q2]) }]});
        }
        {
            var Q0;
            Q0 = qSketchRegion(id + "F6", true);
            extrude(context, id + "F10", {"entities" : qUnion([Q0]), "operationType" : NewBodyOperationType.REMOVE, "oppositeDirection" : true, "depth" : 25 * mm, "offsetDistance" : 25 * mm, "hasSecondDirection" : true, "secondDirectionOppositeDirection" : false, "secondDirectionDepth" : 25 * mm});
        }
        {
            var Q0;
            Q0=qCreatedBy(id+"F2.planeOp",FACE);
            var sketch = newSketch(context, id + "F11", { "sketchPlane" : qUnion([Q0])});
            skLineSegment(sketch, "E345.bottom", {"start": v(35.07, 1.72) * mm, "end": v(38.25, 1.72) * mm});
            skLineSegment(sketch, "E345.top", {"start": v(35.07, -1.46) * mm, "end": v(38.25, -1.46) * mm});
            skLineSegment(sketch, "E345.left", {"start": v(35.07, 1.72) * mm, "end": v(35.07, -1.46) * mm});
            skLineSegment(sketch, "E345.right", {"start": v(38.25, 1.72) * mm, "end": v(38.25, -1.46) * mm});
            skSolve(sketch);
        }
        {
            var Q0;
            Q0=qCreatedBy(makeId("Top.planeOp"),FACE);
            var sketch = newSketch(context, id + "F12", { "sketchPlane" : qUnion([Q0])});
            skLineSegment(sketch, "E346.bottom", {"start": v(109.21, -9.54) * mm, "end": v(106.04, -9.54) * mm});
            skLineSegment(sketch, "E346.top", {"start": v(109.21, -12.71) * mm, "end": v(106.04, -12.71) * mm});
            skLineSegment(sketch, "E346.left", {"start": v(109.21, -9.54) * mm, "end": v(109.21, -12.71) * mm});
            skLineSegment(sketch, "E346.right", {"start": v(106.04, -9.54) * mm, "end": v(106.04, -12.71) * mm});
            skSolve(sketch);
        }
        {
            var Q0;
            Q0 = qSketchRegion(id + "F12", true);
            var Q1;
            Q1 = qSketchRegion(id + "F11", true);
            loft(context, id + "F13", {"operationType" : NewBodyOperationType.REMOVE, "sheetProfilesArray" : [{ "sheetProfileEntities" : qUnion([Q0]) }, { "sheetProfileEntities" : qUnion([Q1]) }]});
        }
        {
            var Q0;
            Q0=makeQuery(id+"F5.opLoft","CAP_FACE",FACE,{"disambiguationData":[OSD([makeQuery(id+"F1.imprint","IMPRINT",FACE,{"disambiguationData":[TD([[makeQuery(id+"F1.imprint","IMPRINT",EDGE,{"derivedFrom":sQuery(id+"F1.wireOp",EDGE,"E193")}),-1.0]])]})])],"isStart":true});
            var sketch = newSketch(context, id + "F14", { "sketchPlane" : qUnion([Q0])});
            skLineSegment(sketch, "E347.bottom", {"start": v(1.49, 2.25) * mm, "end": v(3.73, 0) * mm});
            skLineSegment(sketch, "E347.top", {"start": v(-0.76, 0) * mm, "end": v(1.49, -2.25) * mm});
            skLineSegment(sketch, "E347.left", {"start": v(1.49, 2.25) * mm, "end": v(-0.76, 0) * mm});
            skLineSegment(sketch, "E347.right", {"start": v(3.73, 0) * mm, "end": v(1.49, -2.25) * mm});
            skSolve(sketch);
        }
        {
            var Q0;
            Q0=makeQuery(id+"F5.opLoft","CAP_FACE",FACE,{"disambiguationData":[OSD([makeQuery(id+"F4.imprint","IMPRINT",FACE,{"disambiguationData":[TD([[makeQuery(id+"F4.imprint","IMPRINT",EDGE,{"derivedFrom":sQuery(id+"F4.wireOp",EDGE,"E335")}),-1.0]])]})])],"isStart":true});
            var sketch = newSketch(context, id + "F15", { "sketchPlane" : qUnion([Q0])});
            skLineSegment(sketch, "E348.0", {"start": v(1.72, 2.25) * mm, "end": v(3.96, 0) * mm});
            skLineSegment(sketch, "E348.1", {"start": v(-0.53, 0) * mm, "end": v(1.72, 2.25) * mm});
            skLineSegment(sketch, "E348.2", {"start": v(-0.53, 0) * mm, "end": v(1.72, -2.25) * mm});
            skLineSegment(sketch, "E348.3", {"start": v(1.72, -2.25) * mm, "end": v(3.96, 0) * mm});
            skSolve(sketch);
        }
        {
            var Q0;
            Q0 = qSketchRegion(id + "F14", true);
            var Q1;
            Q1 = qSketchRegion(id + "F15", true);
            loft(context, id + "F16", {"operationType" : NewBodyOperationType.REMOVE, "sheetProfilesArray" : [{ "sheetProfileEntities" : qUnion([Q0]) }, { "sheetProfileEntities" : qUnion([Q1]) }]});
        }
    });
